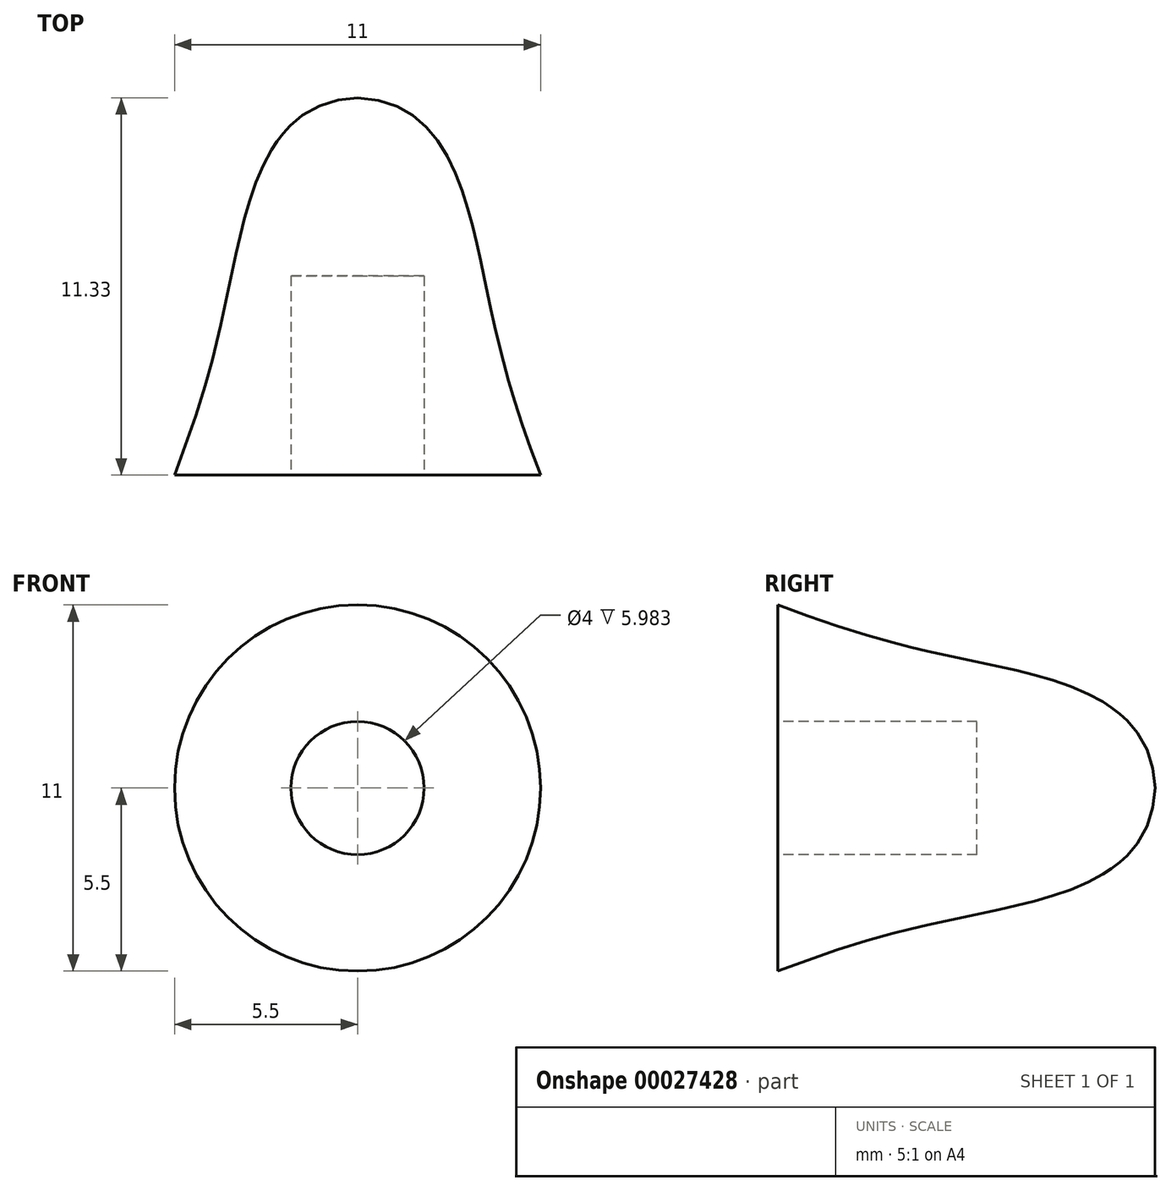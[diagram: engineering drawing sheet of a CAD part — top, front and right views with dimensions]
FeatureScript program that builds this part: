
annotation { "Feature Type Name" : "Feature", "Feature Type Description" : "" }
export const myFeature = defineFeature(function(context is Context, id is Id, definition is map)
    precondition{}
    {
        {
            var Q0;
            Q0=qCreatedBy(makeId("Top.planeOp"),FACE);
            var sketch = newSketch(context, id + "F0", { "sketchPlane" : qUnion([Q0])});
            skLineSegment(sketch, "E0.bottom", {"start": v(0, 0) * mm, "end": v(2, 0) * mm});
            skLineSegment(sketch, "E0.top", {"start": v(0, 5.98) * mm, "end": v(2, 5.98) * mm});
            skLineSegment(sketch, "E0.right", {"start": v(2, 0) * mm, "end": v(2, 5.98) * mm});
            skLineSegment(sketch, "E1.bottom", {"start": v(0, 0) * mm, "end": v(5.5, 0) * mm});
            skLineSegment(sketch, "E1.left", {"start": v(0, 5.98) * mm, "end": v(0, 11.33) * mm});
            skFitSpline(sketch, "E2", {"points": [v(0, 11.33) * mm, v(3.54, 7.13) * mm, v(5.5, 0) * mm], "startDerivative": vector(15.53, -0.48) * mm, "endDerivative": vector(7.33, -19.14) * mm});
            skSolve(sketch);
        }
        {
            var Q0;
            Q0=makeQuery(id+"F0.imprint","IMPRINT",FACE,{"disambiguationData":[TD([[makeQuery(id+"F0.imprint","IMPRINT",EDGE,{"derivedFrom":sQuery(id+"F0.wireOp",EDGE,"E0.top")}),1.0]])]});
            var Q1;
            Q1=sQuery(id+"F0.wireOp",EDGE,"E1.left");
            revolve(context, id + "F1", {"entities" : qUnion([Q0]), "axis" : qUnion([Q1]), "revolveType" : RevolveType.FULL});
        }
    });
